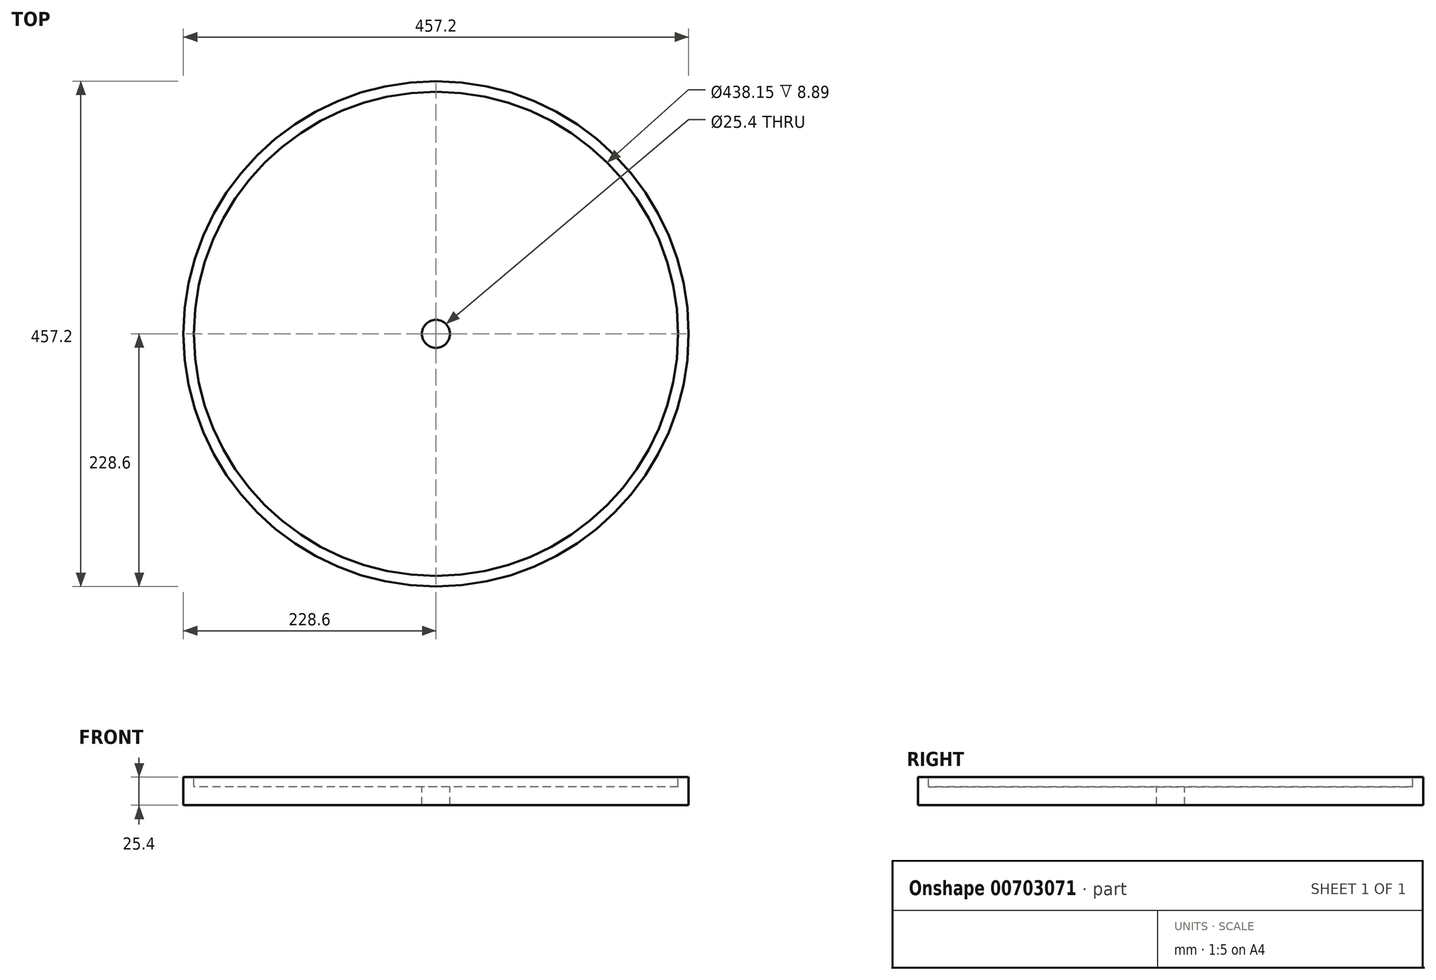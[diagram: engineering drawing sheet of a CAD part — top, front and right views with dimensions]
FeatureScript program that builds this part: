
annotation { "Feature Type Name" : "Feature", "Feature Type Description" : "" }
export const myFeature = defineFeature(function(context is Context, id is Id, definition is map)
    precondition{}
    {
        {
            var Q0;
            Q0=qCreatedBy(makeId("Top.planeOp"),FACE);
            var sketch = newSketch(context, id + "F0", { "sketchPlane" : qUnion([Q0])});
            skCircle(sketch, "E0", {"center": v(0, 0) * mm, "radius": 228.6 * mm});
            skSolve(sketch);
        }
        {
            var Q0;
            Q0=makeQuery(id+"F0.imprint","IMPRINT",FACE,{"disambiguationData":[TD([[makeQuery(id+"F0.imprint","IMPRINT",EDGE,{"derivedFrom":sQuery(id+"F0.wireOp",EDGE,"E0")}),1.0]])]});
            extrude(context, id + "F1", {"entities" : qUnion([Q0]), "oppositeDirection" : true, "depth" : 25.4 * mm, "offsetDistance" : 25.4 * mm});
        }
        {
            var Q0;
            Q0=makeQuery(id+"F1.opExtrude","CAP_FACE",FACE,{"disambiguationData":[OSD([sQuery(id+"F0.wireOp",EDGE,"E0")])],"isStart":true});
            var sketch = newSketch(context, id + "F2", { "sketchPlane" : qUnion([Q0])});
            skCircle(sketch, "E1", {"center": v(0, 0) * mm, "radius": 219.08 * mm});
            skSolve(sketch);
        }
        {
            var Q0;
            Q0=makeQuery(id+"F2.imprint","IMPRINT",FACE,{"disambiguationData":[TD([[makeQuery(id+"F2.imprint","IMPRINT",EDGE,{"derivedFrom":sQuery(id+"F2.wireOp",EDGE,"E1")}),1.0]])]});
            extrude(context, id + "F3", {"entities" : qUnion([Q0]), "operationType" : NewBodyOperationType.REMOVE, "oppositeDirection" : true, "depth" : 2.54 * mm, "offsetDistance" : 25.4 * mm});
        }
        {
            var Q0;
            Q0=makeQuery(id+"F3.boolean.opBoolean","COPY",FACE,{"derivedFrom":makeQuery(id+"F3.opExtrude","CAP_FACE",FACE,{"disambiguationData":[OSD([sQuery(id+"F2.wireOp",EDGE,"E1")])],"isStart":false})});
            var sketch = newSketch(context, id + "F4", { "sketchPlane" : qUnion([Q0])});
            skLineSegment(sketch, "E2", {"start": v(0, 0) * mm, "end": v(0, 203.2) * mm});
            skArc(sketch, "E3.0.startCap", {"start": v(12.7, 0) * mm, "mid": v(0, -12.7) * mm, "end": v(-12.7, 0) * mm});
            skArc(sketch, "E3.0.endCap", {"start": v(-12.7, 203.2) * mm, "mid": v(0, 215.9) * mm, "end": v(12.7, 203.2) * mm});
            skLineSegment(sketch, "E3.0.left", {"start": v(-12.7, 0) * mm, "end": v(-12.7, 203.2) * mm});
            skLineSegment(sketch, "E3.0.right", {"start": v(12.7, 0) * mm, "end": v(12.7, 203.2) * mm});
            skSolve(sketch);
        }
        {
            var Q0;
            Q0=makeQuery(id+"F4.imprint","IMPRINT",FACE,{"disambiguationData":[TD([[makeQuery(id+"F4.imprint","IMPRINT",EDGE,{"derivedFrom":sQuery(id+"F4.wireOp",EDGE,"E3.0.startCap")}),-1.0]])]});
            extrude(context, id + "F5", {"entities" : qUnion([Q0]), "oppositeDirection" : true, "depth" : 6.35 * mm, "offsetDistance" : 25.4 * mm});
        }
        {
            var Q0;
            Q0=qCreatedBy(makeId("Right.planeOp"),FACE);
            var sketch = newSketch(context, id + "F6", { "sketchPlane" : qUnion([Q0])});
            skLineSegment(sketch, "E4", {"start": v(0, 0) * mm, "end": v(0, 91.95) * mm, "construction": true});
            skSolve(sketch);
        }
        {
            var Q0;
            Q0=makeQuery(id+"F5.opExtrude","SWEPT_BODY",BODY,{"disambiguationData":[OSD([sQuery(id+"F4.wireOp",EDGE,"E3.0.startCap"),sQuery(id+"F4.wireOp",EDGE,"E3.0.endCap"),sQuery(id+"F4.wireOp",EDGE,"E3.0.left"),sQuery(id+"F4.wireOp",EDGE,"E3.0.right")])]});
            var Q1;
            Q1=sQuery(id+"F6.wireOp",EDGE,"E4");
            circularPattern(context, id + "F7", {"operationType" : NewBodyOperationType.REMOVE, "entities" : qUnion([Q0]), "axis" : qUnion([Q1]), "angle" : 360 * degree, "instanceCount" : 12, "equalSpace" : true});
        }
        {
            var Q0;
            Q0=qCreatedBy(makeId("Top.planeOp"),FACE);
            var sketch = newSketch(context, id + "F8", { "sketchPlane" : qUnion([Q0])});
            skCircle(sketch, "E5", {"center": v(0, 0) * mm, "radius": 12.7 * mm});
            skSolve(sketch);
        }
        {
            var Q0;
            Q0 = qSketchRegion(id + "F8", true);
            extrude(context, id + "F9", {"entities" : qUnion([Q0]), "operationType" : NewBodyOperationType.REMOVE, "oppositeDirection" : true, "depth" : 25.4 * mm, "offsetDistance" : 25.4 * mm});
        }
    });
